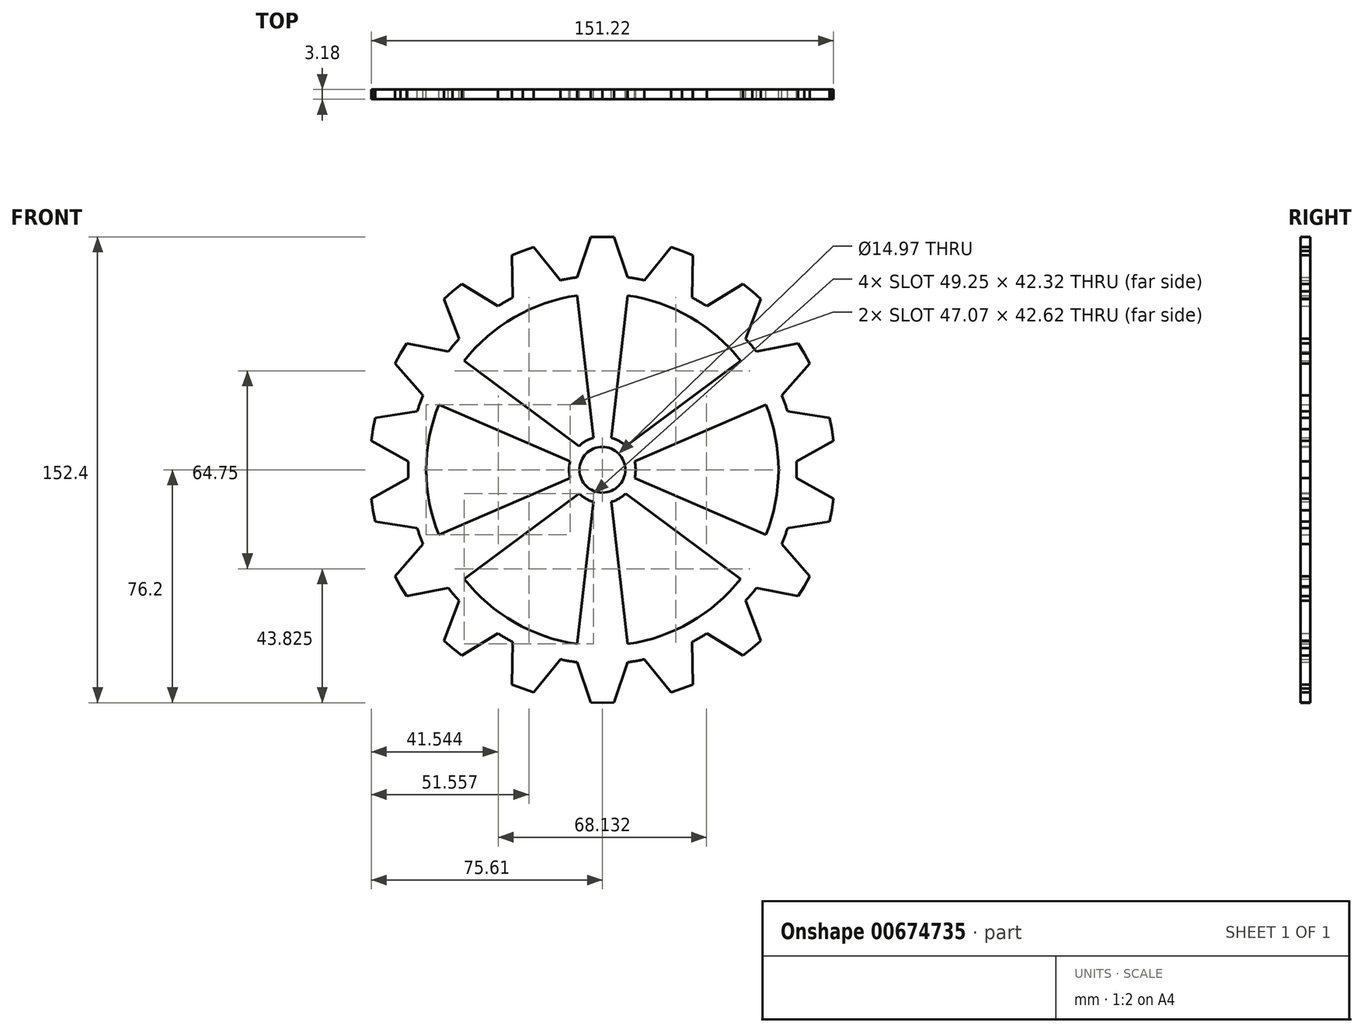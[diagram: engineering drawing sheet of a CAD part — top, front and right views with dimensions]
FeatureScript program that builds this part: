
annotation { "Feature Type Name" : "Feature", "Feature Type Description" : "" }
export const myFeature = defineFeature(function(context is Context, id is Id, definition is map)
    precondition{}
    {
        {
            var Q0;
            Q0=qCreatedBy(makeId("Front.planeOp"),FACE);
            var sketch = newSketch(context, id + "F0", { "sketchPlane" : qUnion([Q0])});
            skCircle(sketch, "E0", {"center": v(0, 0) * mm, "radius": 76.2 * mm, "construction": true});
            skCircle(sketch, "E1", {"center": v(0, 0) * mm, "radius": 63.5 * mm});
            skLineSegment(sketch, "E2", {"start": v(0, 76.2) * mm, "end": v(0, -76.2) * mm, "construction": true});
            skLineSegment(sketch, "E3", {"start": v(0, 76.2) * mm, "end": v(-3.78, 76.1) * mm});
            skLineSegment(sketch, "E4", {"start": v(-3.78, 76.1) * mm, "end": v(-8.3, 62.95) * mm});
            skLineSegment(sketch, "E5.MirrorCS", {"start": v(0, 76.2) * mm, "end": v(3.78, 76.1) * mm});
            skLineSegment(sketch, "E6.MirrorCS", {"start": v(3.78, 76.1) * mm, "end": v(8.3, 62.95) * mm});
            skLineSegment(sketch, "E7.1.0", {"start": v(-29.58, 70.22) * mm, "end": v(-29.33, 56.32) * mm});
            skLineSegment(sketch, "E7.1.1", {"start": v(-26.06, 71.6) * mm, "end": v(-29.58, 70.22) * mm});
            skLineSegment(sketch, "E7.1.2", {"start": v(-26.06, 71.6) * mm, "end": v(-22.48, 72.8) * mm});
            skLineSegment(sketch, "E7.1.3", {"start": v(-22.48, 72.8) * mm, "end": v(-13.73, 62) * mm});
            skLineSegment(sketch, "E7.2.0", {"start": v(-51.82, 55.87) * mm, "end": v(-46.83, 42.89) * mm});
            skLineSegment(sketch, "E7.2.1", {"start": v(-48.98, 58.37) * mm, "end": v(-51.82, 55.87) * mm});
            skLineSegment(sketch, "E7.2.2", {"start": v(-48.98, 58.37) * mm, "end": v(-46.02, 60.73) * mm});
            skLineSegment(sketch, "E7.2.3", {"start": v(-46.02, 60.73) * mm, "end": v(-34.1, 53.56) * mm});
            skLineSegment(sketch, "E7.3.0", {"start": v(-67.8, 34.78) * mm, "end": v(-58.67, 24.29) * mm});
            skLineSegment(sketch, "E7.3.1", {"start": v(-66, 38.1) * mm, "end": v(-67.8, 34.78) * mm});
            skLineSegment(sketch, "E7.3.2", {"start": v(-66, 38.1) * mm, "end": v(-64.02, 41.33) * mm});
            skLineSegment(sketch, "E7.3.3", {"start": v(-64.02, 41.33) * mm, "end": v(-50.37, 38.67) * mm});
            skLineSegment(sketch, "E7.4.0", {"start": v(-75.6, 9.5) * mm, "end": v(-63.44, 2.75) * mm});
            skLineSegment(sketch, "E7.4.1", {"start": v(-75.04, 13.23) * mm, "end": v(-75.6, 9.5) * mm});
            skLineSegment(sketch, "E7.4.2", {"start": v(-75.04, 13.23) * mm, "end": v(-74.3, 16.94) * mm});
            skLineSegment(sketch, "E7.4.3", {"start": v(-74.3, 16.94) * mm, "end": v(-60.56, 19.1) * mm});
            skLineSegment(sketch, "E7.5.0", {"start": v(-74.3, -16.94) * mm, "end": v(-60.56, -19.1) * mm});
            skLineSegment(sketch, "E7.5.1", {"start": v(-75.04, -13.23) * mm, "end": v(-74.3, -16.94) * mm});
            skLineSegment(sketch, "E7.5.2", {"start": v(-75.04, -13.23) * mm, "end": v(-75.6, -9.5) * mm});
            skLineSegment(sketch, "E7.5.3", {"start": v(-75.6, -9.5) * mm, "end": v(-63.44, -2.75) * mm});
            skLineSegment(sketch, "E7.6.0", {"start": v(-64.02, -41.33) * mm, "end": v(-50.37, -38.67) * mm});
            skLineSegment(sketch, "E7.6.1", {"start": v(-66, -38.1) * mm, "end": v(-64.02, -41.33) * mm});
            skLineSegment(sketch, "E7.6.2", {"start": v(-66, -38.1) * mm, "end": v(-67.8, -34.78) * mm});
            skLineSegment(sketch, "E7.6.3", {"start": v(-67.8, -34.78) * mm, "end": v(-58.67, -24.29) * mm});
            skLineSegment(sketch, "E7.7.0", {"start": v(-46.02, -60.73) * mm, "end": v(-34.1, -53.56) * mm});
            skLineSegment(sketch, "E7.7.1", {"start": v(-48.98, -58.37) * mm, "end": v(-46.02, -60.73) * mm});
            skLineSegment(sketch, "E7.7.2", {"start": v(-48.98, -58.37) * mm, "end": v(-51.82, -55.87) * mm});
            skLineSegment(sketch, "E7.7.3", {"start": v(-51.82, -55.87) * mm, "end": v(-46.83, -42.89) * mm});
            skLineSegment(sketch, "E7.8.0", {"start": v(-22.48, -72.8) * mm, "end": v(-13.73, -62) * mm});
            skLineSegment(sketch, "E7.8.1", {"start": v(-26.06, -71.6) * mm, "end": v(-22.48, -72.8) * mm});
            skLineSegment(sketch, "E7.8.2", {"start": v(-26.06, -71.6) * mm, "end": v(-29.58, -70.22) * mm});
            skLineSegment(sketch, "E7.8.3", {"start": v(-29.58, -70.22) * mm, "end": v(-29.33, -56.32) * mm});
            skLineSegment(sketch, "E7.9.0", {"start": v(3.78, -76.1) * mm, "end": v(8.3, -62.95) * mm});
            skLineSegment(sketch, "E7.9.1", {"start": v(0, -76.2) * mm, "end": v(3.78, -76.1) * mm});
            skLineSegment(sketch, "E7.9.2", {"start": v(0, -76.2) * mm, "end": v(-3.78, -76.1) * mm});
            skLineSegment(sketch, "E7.9.3", {"start": v(-3.78, -76.1) * mm, "end": v(-8.3, -62.95) * mm});
            skLineSegment(sketch, "E7.10.0", {"start": v(29.58, -70.22) * mm, "end": v(29.33, -56.32) * mm});
            skLineSegment(sketch, "E7.10.1", {"start": v(26.06, -71.6) * mm, "end": v(29.58, -70.22) * mm});
            skLineSegment(sketch, "E7.10.2", {"start": v(26.06, -71.6) * mm, "end": v(22.48, -72.8) * mm});
            skLineSegment(sketch, "E7.10.3", {"start": v(22.48, -72.8) * mm, "end": v(13.73, -62) * mm});
            skLineSegment(sketch, "E7.11.0", {"start": v(51.82, -55.87) * mm, "end": v(46.83, -42.89) * mm});
            skLineSegment(sketch, "E7.11.1", {"start": v(48.98, -58.37) * mm, "end": v(51.82, -55.87) * mm});
            skLineSegment(sketch, "E7.11.2", {"start": v(48.98, -58.37) * mm, "end": v(46.02, -60.73) * mm});
            skLineSegment(sketch, "E7.11.3", {"start": v(46.02, -60.73) * mm, "end": v(34.1, -53.56) * mm});
            skLineSegment(sketch, "E7.12.0", {"start": v(67.8, -34.78) * mm, "end": v(58.67, -24.29) * mm});
            skLineSegment(sketch, "E7.12.1", {"start": v(66, -38.1) * mm, "end": v(67.8, -34.78) * mm});
            skLineSegment(sketch, "E7.12.2", {"start": v(66, -38.1) * mm, "end": v(64.02, -41.33) * mm});
            skLineSegment(sketch, "E7.12.3", {"start": v(64.02, -41.33) * mm, "end": v(50.37, -38.67) * mm});
            skLineSegment(sketch, "E7.13.0", {"start": v(75.6, -9.5) * mm, "end": v(63.44, -2.75) * mm});
            skLineSegment(sketch, "E7.13.1", {"start": v(75.04, -13.23) * mm, "end": v(75.6, -9.5) * mm});
            skLineSegment(sketch, "E7.13.2", {"start": v(75.04, -13.23) * mm, "end": v(74.3, -16.94) * mm});
            skLineSegment(sketch, "E7.13.3", {"start": v(74.3, -16.94) * mm, "end": v(60.56, -19.1) * mm});
            skLineSegment(sketch, "E7.14.0", {"start": v(74.3, 16.94) * mm, "end": v(60.56, 19.1) * mm});
            skLineSegment(sketch, "E7.14.1", {"start": v(75.04, 13.23) * mm, "end": v(74.3, 16.94) * mm});
            skLineSegment(sketch, "E7.14.2", {"start": v(75.04, 13.23) * mm, "end": v(75.6, 9.5) * mm});
            skLineSegment(sketch, "E7.14.3", {"start": v(75.6, 9.5) * mm, "end": v(63.44, 2.75) * mm});
            skLineSegment(sketch, "E7.15.0", {"start": v(64.02, 41.33) * mm, "end": v(50.37, 38.67) * mm});
            skLineSegment(sketch, "E7.15.1", {"start": v(66, 38.1) * mm, "end": v(64.02, 41.33) * mm});
            skLineSegment(sketch, "E7.15.2", {"start": v(66, 38.1) * mm, "end": v(67.8, 34.78) * mm});
            skLineSegment(sketch, "E7.15.3", {"start": v(67.8, 34.78) * mm, "end": v(58.67, 24.29) * mm});
            skLineSegment(sketch, "E7.16.0", {"start": v(46.02, 60.73) * mm, "end": v(34.1, 53.56) * mm});
            skLineSegment(sketch, "E7.16.1", {"start": v(48.98, 58.37) * mm, "end": v(46.02, 60.73) * mm});
            skLineSegment(sketch, "E7.16.2", {"start": v(48.98, 58.37) * mm, "end": v(51.82, 55.87) * mm});
            skLineSegment(sketch, "E7.16.3", {"start": v(51.82, 55.87) * mm, "end": v(46.83, 42.89) * mm});
            skLineSegment(sketch, "E7.17.0", {"start": v(22.48, 72.8) * mm, "end": v(13.73, 62) * mm});
            skLineSegment(sketch, "E7.17.1", {"start": v(26.06, 71.6) * mm, "end": v(22.48, 72.8) * mm});
            skLineSegment(sketch, "E7.17.2", {"start": v(26.06, 71.6) * mm, "end": v(29.58, 70.22) * mm});
            skLineSegment(sketch, "E7.17.3", {"start": v(29.58, 70.22) * mm, "end": v(29.33, 56.32) * mm});
            skCircle(sketch, "E8", {"center": v(0, 0) * mm, "radius": 10.88 * mm});
            skCircle(sketch, "E9", {"center": v(0, 0) * mm, "radius": 57.6 * mm});
            skLineSegment(sketch, "E10", {"start": v(8.3, 57) * mm, "end": v(2.9, 10.49) * mm});
            skLineSegment(sketch, "E11.MirrorCS", {"start": v(-8.3, 57) * mm, "end": v(-2.9, 10.49) * mm});
            skLineSegment(sketch, "E12.1.0", {"start": v(-45.21, 35.7) * mm, "end": v(-7.64, 7.75) * mm});
            skLineSegment(sketch, "E12.1.1", {"start": v(-53.51, 21.3) * mm, "end": v(-10.53, 2.74) * mm});
            skLineSegment(sketch, "E12.2.0", {"start": v(-53.51, -21.3) * mm, "end": v(-10.53, -2.74) * mm});
            skLineSegment(sketch, "E12.2.1", {"start": v(-45.21, -35.7) * mm, "end": v(-7.64, -7.75) * mm});
            skLineSegment(sketch, "E12.3.0", {"start": v(-8.3, -57) * mm, "end": v(-2.9, -10.49) * mm});
            skLineSegment(sketch, "E12.3.1", {"start": v(8.3, -57) * mm, "end": v(2.9, -10.49) * mm});
            skLineSegment(sketch, "E12.4.0", {"start": v(45.21, -35.7) * mm, "end": v(7.64, -7.75) * mm});
            skLineSegment(sketch, "E12.4.1", {"start": v(53.51, -21.3) * mm, "end": v(10.53, -2.74) * mm});
            skLineSegment(sketch, "E12.5.0", {"start": v(53.51, 21.3) * mm, "end": v(10.53, 2.74) * mm});
            skLineSegment(sketch, "E12.5.1", {"start": v(45.21, 35.7) * mm, "end": v(7.64, 7.75) * mm});
            skCircle(sketch, "E13", {"center": v(0, 0) * mm, "radius": 7.49 * mm});
            skSolve(sketch);
        }
        {
            var Q0;
            Q0 = qSketchRegion(id + "F0", true);
            var Q1;
            {var subQ0=sQuery(id+"F0.wireOp",EDGE,"E10");Q1=makeQuery(id+"F0.imprint","IMPRINT",FACE,{"disambiguationData":[TD([[makeQuery(id+"F0.imprint","IMPRINT",EDGE,{"derivedFrom":subQ0}),-1.0]])]});}
            var Q2;
            {var subQ0=sQuery(id+"F0.wireOp",EDGE,"E12.5.0");Q2=makeQuery(id+"F0.imprint","IMPRINT",FACE,{"disambiguationData":[TD([[makeQuery(id+"F0.imprint","IMPRINT",EDGE,{"derivedFrom":subQ0}),-1.0]])]});}
            var Q3;
            {var subQ0=sQuery(id+"F0.wireOp",EDGE,"E12.4.0");Q3=makeQuery(id+"F0.imprint","IMPRINT",FACE,{"disambiguationData":[TD([[makeQuery(id+"F0.imprint","IMPRINT",EDGE,{"derivedFrom":subQ0}),-1.0]])]});}
            var Q4;
            {var subQ0=sQuery(id+"F0.wireOp",EDGE,"E12.3.0");Q4=makeQuery(id+"F0.imprint","IMPRINT",FACE,{"disambiguationData":[TD([[makeQuery(id+"F0.imprint","IMPRINT",EDGE,{"derivedFrom":subQ0}),-1.0]])]});}
            var Q5;
            {var subQ0=sQuery(id+"F0.wireOp",EDGE,"E12.2.0");Q5=makeQuery(id+"F0.imprint","IMPRINT",FACE,{"disambiguationData":[TD([[makeQuery(id+"F0.imprint","IMPRINT",EDGE,{"derivedFrom":subQ0}),-1.0]])]});}
            var Q6;
            {var subQ0=sQuery(id+"F0.wireOp",EDGE,"E12.1.0");Q6=makeQuery(id+"F0.imprint","IMPRINT",FACE,{"disambiguationData":[TD([[makeQuery(id+"F0.imprint","IMPRINT",EDGE,{"derivedFrom":subQ0}),-1.0]])]});}
            var Q7;
            {var subQ0=sQuery(id+"F0.wireOp",EDGE,"E8");var subQ8=makeQuery(id+"F0.imprint","INTERSECT",VERTEX,{"derivedFrom":[subQ0,sQuery(id+"F0.wireOp",EDGE,"E12.5.0")]});Q7=makeQuery(id+"F0.imprint","IMPRINT",FACE,{"disambiguationData":[TD([[makeQuery(id+"F0.imprint","IMPRINT",EDGE,{"disambiguationData":[TD([[subQ8,-1.0]])],"derivedFrom":subQ0}),1.0]])]});}
            extrude(context, id + "F1", {"entities" : qUnion([Q0, Q1, Q2, Q3, Q4, Q5, Q6, Q7]), "depth" : 3.17 * mm, "offsetDistance" : 25.4 * mm});
        }
    });
